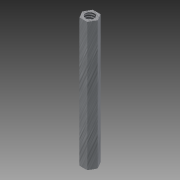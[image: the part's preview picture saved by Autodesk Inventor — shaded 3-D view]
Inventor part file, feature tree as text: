
AUTODESK INVENTOR PART (.ipt)
format: ipt  version: 2012 (Build 160160000, 160)  size: 114,176 bytes
history: native  units: in
note: dims shown in document units (in); Inventor stores cm internally (conversion verified against a paired STEP export)
features: thread x2, other x1, imported_body x1, plane x1, split x1
ambient origin geometry x8: Origin, YZ Plane, XZ Plane, XY Plane, X Axis, Y Axis, Z Axis, Center Point
feature tree (6):
  parser-record x1  (decoder bookkeeping rows leaked as tree rows — omitted from the tree; the rows remain in map.json)
  imported_body  "Base1"
  thread  "Thread1"  [1 undecoded]
  thread  "Thread2"  [1 undecoded]
  plane  "Work Plane1"
  split  "Split1"
note: 2 required parameter values undecoded (feature->parameter linkage not recoverable at this tier; creation-order binding heuristic only, values carry confidence <= 0.55)
